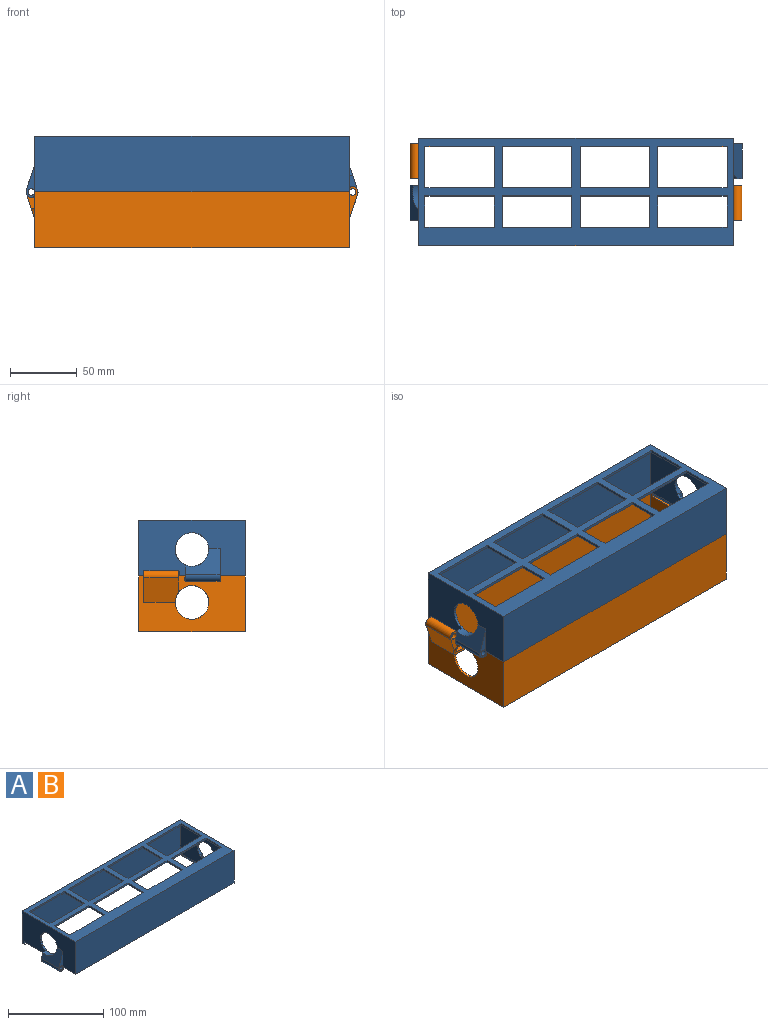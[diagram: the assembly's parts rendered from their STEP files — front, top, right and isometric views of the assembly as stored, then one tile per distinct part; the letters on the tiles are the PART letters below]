
ASSEMBLY  parts=2 mates=1
PART A: 80 faces, bbox 248.4x80x45.7 mm
  f0: plane 235.2x4mm, normal (0,0,-1), area 383.4mm2, adj f1,f4,f5,f7,f8,f10,f32,f77
  f1: plane 76.8x39.6mm, normal (1,0,0), area 2379.8mm2, adj f0,f2,f6,f10,f11,f12,f14,f15
  f2: plane 235.2x19mm, normal (0,0,-1), area 458.4mm2, adj f1,f4,f5,f7,f9,f11,f20,f21
  f3: plane 4.6x1.6mm, normal (0,0,-1), area 7.4mm2, adj f5,f7,f31,f74
  f4: plane 80x41.6mm, normal (-1,0,0), area 2400.3mm2, adj f0,f2,f6,f8,f9,f65,f69,f70
  f5: plane 80x41.6mm, normal (1,0,0), area 2239.7mm2, adj f0,f2,f3,f8,f9,f28,f31,f32
  f6: plane 4.6x1.6mm, normal (0,0,-1), area 7.4mm2, adj f1,f4,f71,f78
  f7: plane 76.8x39.6mm, normal (-1,0,0), area 2382.5mm2, adj f0,f2,f3,f10,f11,f16,f18,f19
  f8: plane 235.2x41.6mm, normal (0,1,0), area 9784.3mm2, adj f0,f4,f5,f65
  f9: plane 235.2x41.6mm, normal (0,-1,0), area 9784.3mm2, adj f2,f4,f5,f65
  f10: plane 232x39.6mm, normal (0,-1,0), area 9187.2mm2, adj f0,f1,f7,f66
  f11: plane 232x39.6mm, normal (0,1,0), area 9187.2mm2, adj f1,f2,f7,f66
  f12: plane 6x3mm, normal (0,-1,0), area 18mm2, adj f1,f13,f15,f66
  f13: plane 6x3mm, normal (1,0,0), area 18mm2, adj f12,f14,f15,f66
  f14: plane 6x3mm, normal (0.71,0.71,0), area 25.5mm2, adj f1,f13,f15,f66
  f15: plane 6x3mm, normal (0,0,-1), area 13.5mm2, adj f1,f12,f13,f14
  f16: plane 6x3mm, normal (-0.71,0.71,0), area 25.5mm2, adj f7,f17,f19,f66
  f17: plane 6x3mm, normal (-1,0,0), area 18mm2, adj f16,f18,f19,f66
  f18: plane 6x3mm, normal (0,-1,0), area 18mm2, adj f7,f17,f19,f66
  f19: plane 6x3mm, normal (0,0,-1), area 13.5mm2, adj f7,f16,f17,f18
  f20: plane 6x3mm, normal (0,-1,0), area 18mm2, adj f1,f2,f21,f23
  f21: plane 6x3mm, normal (1,0,0), area 18mm2, adj f2,f20,f22,f23
  f22: plane 6x3mm, normal (0.71,0.71,0), area 25.5mm2, adj f1,f2,f21,f23
  f23: plane 6x3mm, normal (0,0,1), area 13.5mm2, adj f1,f20,f21,f22
  f24: plane 6x3mm, normal (-0.71,0.71,0), area 25.5mm2, adj f2,f7,f25,f27
  f25: plane 6x3mm, normal (-1,0,0), area 18mm2, adj f2,f24,f26,f27
  f26: plane 6x3mm, normal (0,-1,0), area 18mm2, adj f2,f7,f25,f27
  f27: plane 6x3mm, normal (0,0,1), area 13.5mm2, adj f7,f24,f25,f26
  f28: plane 26x18.39mm, normal (0.95,0,0.33), area 491.9mm2, adj f5,f29,f31,f32,f73
  f29: cylinder r=4.1mm len=26mm, axis (0,1,0), area 372.2mm2, adj f7,f28,f31,f32
  f30: cylinder r=2.5mm len=26mm, axis (0,1,0), area 408.4mm2, adj f31,f32
  f31: plane 16.3x8.2mm, normal (0,-1,0), area 64.4mm2, adj f3,f5,f28,f29,f30,f73
  f32: plane 23.9x8.2mm, normal (0,1,0), area 74.3mm2, adj f0,f5,f28,f29,f30
  f33: plane 52x2mm, normal (0,-1,0), area 104mm2, adj f34,f64,f65,f66
  f34: plane 31x2mm, normal (-1,0,0), area 62mm2, adj f33,f35,f65,f66
  f35: plane 52x2mm, normal (0,1,0), area 104mm2, adj f34,f64,f65,f66
  f36: plane 52x2mm, normal (0,-1,0), area 104mm2, adj f37,f57,f65,f66
  f37: plane 31x2mm, normal (-1,0,0), area 62mm2, adj f36,f38,f65,f66
  f38: plane 52x2mm, normal (0,1,0), area 104mm2, adj f37,f57,f65,f66
  f39: plane 52x2mm, normal (0,1,0), area 104mm2, adj f40,f58,f65,f66
  f40: plane 31x2mm, normal (1,0,0), area 62mm2, adj f39,f41,f65,f66
  f41: plane 52x2mm, normal (0,-1,0), area 104mm2, adj f40,f58,f65,f66
  f42: plane 31x2mm, normal (-1,0,0), area 62mm2, adj f43,f59,f65,f66
  f43: plane 52x2mm, normal (0,1,0), area 104mm2, adj f42,f44,f65,f66
  f44: plane 31x2mm, normal (1,0,0), area 62mm2, adj f43,f59,f65,f66
  f45: plane 52x2mm, normal (0,1,0), area 104mm2, adj f46,f60,f65,f66
  f46: plane 23.4x2mm, normal (1,0,0), area 46.8mm2, adj f45,f47,f65,f66
  f47: plane 52x2mm, normal (0,-1,0), area 104mm2, adj f46,f60,f65,f66
  f48: plane 52x2mm, normal (0,1,0), area 104mm2, adj f49,f61,f65,f66
  f49: plane 23.4x2mm, normal (1,0,0), area 46.8mm2, adj f48,f50,f65,f66
  f50: plane 52x2mm, normal (0,-1,0), area 104mm2, adj f49,f61,f65,f66
  f51: plane 23.4x2mm, normal (-1,0,0), area 46.8mm2, adj f52,f62,f65,f66
  f52: plane 52x2mm, normal (0,1,0), area 104mm2, adj f51,f53,f65,f66
  f53: plane 23.4x2mm, normal (1,0,0), area 46.8mm2, adj f52,f62,f65,f66
  f54: plane 52x2mm, normal (0,1,0), area 104mm2, adj f55,f63,f65,f66
  f55: plane 23.4x2mm, normal (1,0,0), area 46.8mm2, adj f54,f56,f65,f66
  f56: plane 52x2mm, normal (0,-1,0), area 104mm2, adj f55,f63,f65,f66
  f57: plane 31x2mm, normal (1,0,0), area 62mm2, adj f36,f38,f65,f66
  f58: plane 31x2mm, normal (-1,0,0), area 62mm2, adj f39,f41,f65,f66
  f59: plane 52x2mm, normal (0,-1,0), area 104mm2, adj f42,f44,f65,f66
  f60: plane 23.4x2mm, normal (-1,0,0), area 46.8mm2, adj f45,f47,f65,f66
  f61: plane 23.4x2mm, normal (-1,0,0), area 46.8mm2, adj f48,f50,f65,f66
  f62: plane 52x2mm, normal (0,-1,0), area 104mm2, adj f51,f53,f65,f66
  f63: plane 23.4x2mm, normal (-1,0,0), area 46.8mm2, adj f54,f56,f65,f66
  f64: plane 31x2mm, normal (1,0,0), area 62mm2, adj f33,f35,f65,f66
  f65: plane 235.2x80mm, normal (0,0,1), area 7500.8mm2, adj f4,f5,f8,f9,f33,f34,f35,f36
  f66: plane 232x76.8mm, normal (0,0,-1), area 6475.4mm2, adj f1,f7,f10,f11,f12,f13,f14,f16
  f67: cylinder r=4.1mm len=26mm, axis (0,1,0), area 368.6mm2, adj f1,f69,f70,f71
  f68: cylinder r=2.5mm len=26mm, axis (0,1,0), area 408.4mm2, adj f70,f71
  f69: plane 26x19.52mm, normal (-0.95,0,0.31), area 321mm2, adj f4,f67,f70,f71,f72
  f70: plane 24.9x8.2mm, normal (0,-1,0), area 77.5mm2, adj f2,f4,f67,f68,f69
  f71: plane 12.38x8.2mm, normal (0,1,0), area 51.9mm2, adj f4,f6,f67,f68,f69,f72
  f72: cylinder r=12.56mm len=25.12mm, axis (-1,0,0), area 206.9mm2, adj f1,f4,f69,f71
  f73: cylinder r=12.56mm len=25.12mm, axis (-1,0,0), area 137.4mm2, adj f5,f7,f28,f31
  f74: plane 3.4x1.6mm, normal (0,-1,0), area 5.4mm2, adj f3,f5,f7,f75
  f75: plane 26.8x1.6mm, normal (0,0,-1), area 42.9mm2, adj f5,f7,f74,f76
  f76: plane 3.4x1.6mm, normal (0,1,0), area 5.4mm2, adj f2,f5,f7,f75
  f77: plane 3.5x1.6mm, normal (0,-1,0), area 5.6mm2, adj f0,f1,f4,f79
  f78: plane 3.5x1.6mm, normal (0,1,0), area 5.6mm2, adj f1,f4,f6,f79
  f79: plane 26.8x1.6mm, normal (0,0,-1), area 42.9mm2, adj f1,f4,f77,f78
PART B: same geometry as A
PLACE A t=(111.8,119.4,83.33)mm
PLACE B rot(axis=(0,1,0),180deg) t=(111.8,119.4,43.73)mm
MATE cylindrical B.f29 <-> A.f67  axis (0,-1,0) through (-8.3,129.4,63.53)mm
